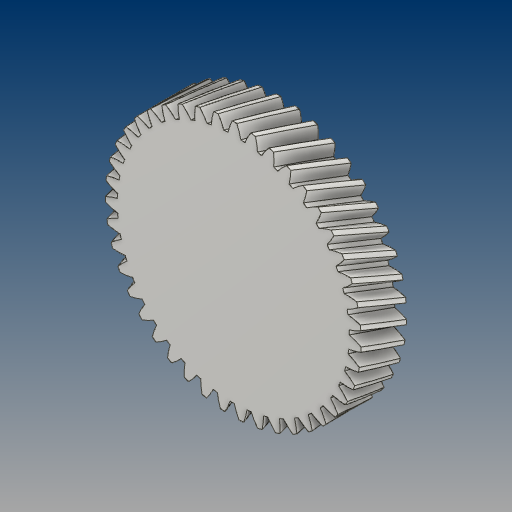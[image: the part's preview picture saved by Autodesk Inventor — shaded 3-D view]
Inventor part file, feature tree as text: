
AUTODESK INVENTOR PART (.ipt)
format: ipt  version: 2021 (Build 250183000, 183)  size: 689,152 bytes
history: native  units: mm (DEFAULTED — no unit token found)
features: plane x3, other x3, sketch x2, extrude x1
ambient origin geometry x8: Origin, YZ Plane, XZ Plane, XY Plane, X Axis, Y Axis, Z Axis, Center Point
bodies: Solid1 (feature_tree)
feature tree (9):
  extrude  "Extrusion1"  Depth=15.0mm TaperAngle=0.0deg
  plane  "Work Plane2"
  plane  "Work Plane8"
  plane  "Work Plane9"
  other  "Spur Gear"
  sketch  "Sketch1"  dims[d0=84.391467mm d1=15.0mm d2=0.0mm]
  sketch  "Sketch2"  dims[d3=80.079377mm d4=10.0mm d5=0.0mm d16=60.0mm d17=0.0mm d34=0.730603mm d39=0.0mm d41=0.0mm d43=60.0mm d46=60.0mm d47=0.0mm d48=0.0mm]
  other  "Srf1"
  other  "Pitch Diameter"
